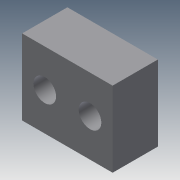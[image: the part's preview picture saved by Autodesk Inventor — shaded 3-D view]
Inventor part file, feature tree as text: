
AUTODESK INVENTOR PART (.ipt)
format: ipt  version: 2013 (Build 170138000, 138)  size: 98,816 bytes
history: native  units: mm
features: extrude x4, sketch x4
ambient origin geometry x8: Origin, YZ Plane, XZ Plane, XY Plane, X Axis, Y Axis, Z Axis, Center Point
bodies: Solid1 (feature_tree)
feature tree (8):
  extrude  "Extrusion1"  Depth=10.0mm
  extrude  "Extrusion2"  Depth=3.0mm
  extrude  "Extrusion3"  Depth=3.0mm
  extrude  "Extrusion4"  Depth=6.0mm TaperAngle=0.0deg
  sketch  "Sketch1"  dims[d0=12.0mm d1=10.0mm]
  sketch  "Sketch2"  dims[d2=6.0mm d3=0.0mm d4=3.0mm]
  sketch  "Sketch3"  dims[d5=3.0mm d6=3.0mm]
  sketch  "Sketch4"  dims[d7=3.0mm d8=6.0mm d9=0.0mm d10=6.0mm d11=0.0mm d12=3.0mm d13=6.0mm d14=3.0mm d15=3.0mm d16=6.0mm d17=0.0mm]
